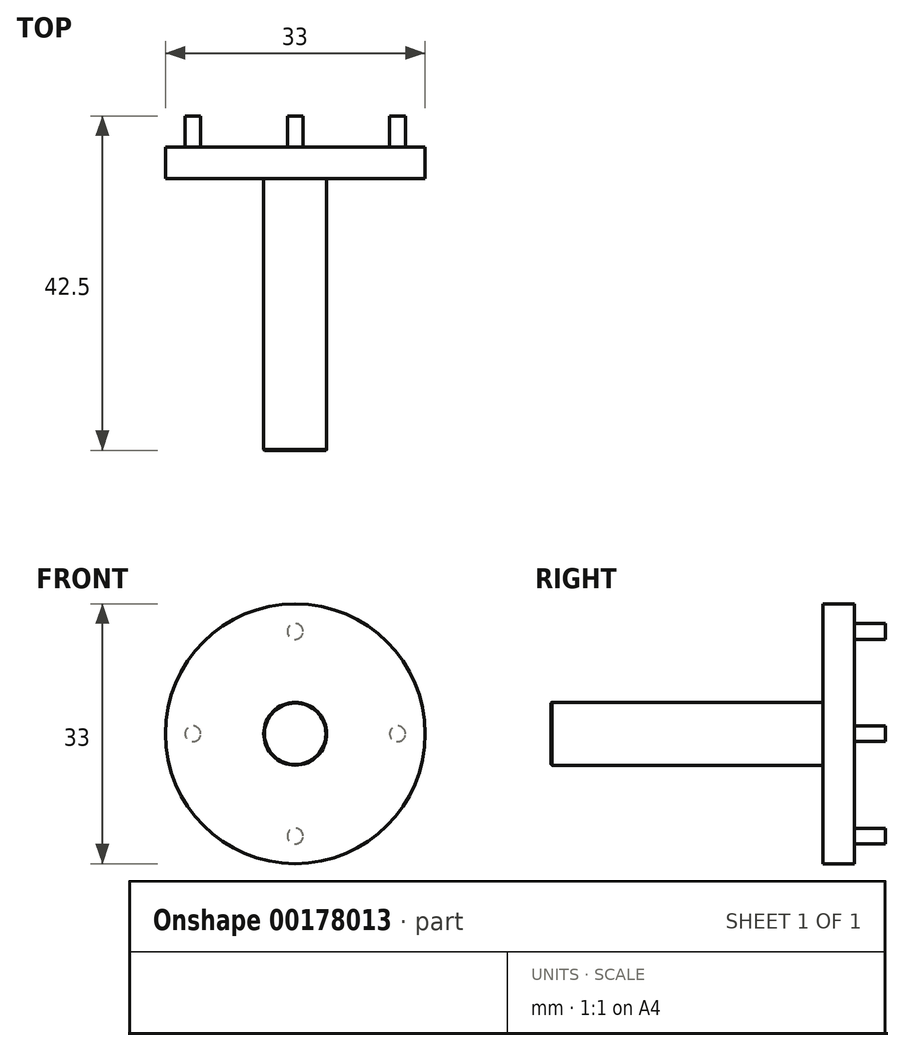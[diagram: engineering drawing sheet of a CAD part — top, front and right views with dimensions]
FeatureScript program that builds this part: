
annotation { "Feature Type Name" : "Feature", "Feature Type Description" : "" }
export const myFeature = defineFeature(function(context is Context, id is Id, definition is map)
    precondition{}
    {
        {
            var Q0;
            Q0=qCreatedBy(makeId("Front.planeOp"),FACE);
            var sketch = newSketch(context, id + "F0", { "sketchPlane" : qUnion([Q0])});
            skCircle(sketch, "E0", {"center": v(0, 0) * mm, "radius": 4 * mm});
            skSolve(sketch);
        }
        {
            var Q0;
            Q0=qSketchRegion(id+"F0",true);
            extrude(context, id + "F1", {"entities" : qUnion([Q0]), "oppositeDirection" : true, "depth" : 28 * mm});
        }
        {
            var Q0;
            Q0=makeQuery(id+"F1.opExtrude","CAP_EDGE",EDGE,{"disambiguationData":[OSD([sQuery(id+"F0.wireOp",EDGE,"E0")])],"isStart":true});
            var Q1;
            Q1=makeQuery(id+"FUtoNcgm9d2VMST_1.boolean.opBoolean","COPY",EDGE,{"derivedFrom":makeQuery(id+"FUtoNcgm9d2VMST_1.opExtrude","SWEPT_EDGE",EDGE,{"disambiguationData":[OSD([sQuery(id+"FhsX1SKP70KWPpT_1.wireOp",EDGE,"66dfabca-b6ee-49d4-a843-992de31440f3.top"),sQuery(id+"FhsX1SKP70KWPpT_1.wireOp",EDGE,"66dfabca-b6ee-49d4-a843-992de31440f3.left")])]})});
            chamfer(context, id + "F2", {"entities" : qUnion([Q0, Q1]), "width" : 0.1 * mm, "tangentPropagation" : true});
        }
        {
            var Q0;
            Q0=makeQuery(id+"F1.opExtrude","CAP_FACE",FACE,{"disambiguationData":[OSD([sQuery(id+"F0.wireOp",EDGE,"E0")])],"isStart":false});
            var sketch = newSketch(context, id + "F3", { "sketchPlane" : qUnion([Q0])});
            skCircle(sketch, "E1", {"center": v(0, 0) * mm, "radius": 4 * mm});
            skSolve(sketch);
        }
        {
            var Q0;
            Q0=qSketchRegion(id+"F3",true);
            extrude(context, id + "F4", {"entities" : qUnion([Q0]), "operationType" : NewBodyOperationType.ADD, "depth" : 6.5 * mm});
        }
        {
            var Q0;
            Q0=makeQuery(id+"F4.opExtrude","CAP_FACE",FACE,{"disambiguationData":[OSD([sQuery(id+"F3.wireOp",EDGE,"E1")])],"isStart":false});
            var sketch = newSketch(context, id + "F5", { "sketchPlane" : qUnion([Q0])});
            skCircle(sketch, "E2", {"center": v(0, 0) * mm, "radius": 16.5 * mm});
            skSolve(sketch);
        }
        {
            var Q0;
            Q0=qSketchRegion(id+"F5",true);
            extrude(context, id + "F6", {"entities" : qUnion([Q0]), "operationType" : NewBodyOperationType.ADD, "depth" : 4 * mm});
        }
        {
            var Q0;
            Q0=makeQuery(id+"F6.opExtrude","CAP_FACE",FACE,{"disambiguationData":[OSD([sQuery(id+"F5.wireOp",EDGE,"E2")])],"isStart":false});
            var sketch = newSketch(context, id + "F7", { "sketchPlane" : qUnion([Q0])});
            skLineSegment(sketch, "E3", {"start": v(0, 0) * mm, "end": v(0, 14.3) * mm, "construction": true});
            skCircle(sketch, "E4", {"center": v(0, 13) * mm, "radius": 1 * mm});
            skCircle(sketch, "E5.1.0", {"center": v(-13, 0) * mm, "radius": 1 * mm});
            skCircle(sketch, "E5.2.0", {"center": v(0, -13) * mm, "radius": 1 * mm});
            skPoint(sketch, "E5.center", {"position": v(0, 0) * mm});
            skCircle(sketch, "E6.1.3.0", {"center": v(13, 0) * mm, "radius": 1 * mm});
            skSolve(sketch);
        }
        {
            var Q0;
            Q0=qSketchRegion(id+"F7",true);
            extrude(context, id + "F8", {"entities" : qUnion([Q0]), "operationType" : NewBodyOperationType.ADD, "depth" : 4 * mm});
        }
    });
